# Revit family: SHR700-SER700
name_source: partatom
category: Mechanical Equipment
revit_build: Autodesk Revit 2016 (Build: 20170117_1200(x64)
units: mm (PartAtom-declared; Revit-internal decimal feet)

## family parameters
Always vertical = Yes
Cut with Voids When Loaded = No
OmniClass Number = 23.75.00.00
OmniClass Title = Climate Control (HVAC)
Part Type = Normal
Room Calculation Point = No
Round Connector Dimension = Use Diameter
Shared = No
Work Plane-Based = No

## types (3) — shared parameters
Apparent Load = 710 W
Current = 5.92 A
Load Classification = HVAC
Manufacturer = Fantech
Power Factor = 1
URL = http://www.fantech.net
Voltage = 120 V
Width = 355.6 mm  [stored 1.16667 ft]

## per-type parameters (varying)
| type | Average Airflow | BPM | Description | Model | Not BPM | Product Number | Weight | construction |
| SER 700 | 707 CFM | No | Light Commercial Energy Recovery Ventilators | SER 700 | Yes | 99276 | 169 lbs | 0 |
| SHR 700 | 723 CFM | No | Commercial Heat Recovery Ventilators | SHR 700 | Yes | 99268 | 185 lbs | 0 |
| SHR 700 BPM | 707 CFM | Yes | Commercial Heat Recovery Ventilators | SHR 700 | No | 99268 | 185 lbs | 99 |

note: [stored X ft] marks values corroborated as IEEE doubles in the binary element streams (Revit-internal decimal feet)

## geometry (parser evidence)
native form markers: Blend x2, Sweep x3
no freeform markers — native parametric forms only
